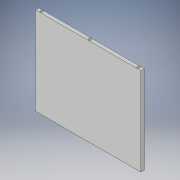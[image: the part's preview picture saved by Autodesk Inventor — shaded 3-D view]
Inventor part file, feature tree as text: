
AUTODESK INVENTOR PART (.ipt)
format: ipt  version: 2019 (Build 230136000, 136)  size: 108,544 bytes
history: native  units: mm
features: extrude x2, sketch x2
ambient origin geometry x8: Origin, YZ Plane, XZ Plane, XY Plane, X Axis, Y Axis, Z Axis, Center Point
bodies: Solid1 (feature_tree)
feature tree (4):
  extrude  "Extrusion1"  Depth=250.0mm
  extrude  "Extrusion2"  Depth=10.0mm
  sketch  "Sketch1"  dims[d0=300.0mm d1=250.0mm]
  sketch  "Sketch4"  dims[d2=162.5mm d3=125.0mm d4=10.0mm d5=0.0mm d6=7.0mm d7=7.0mm d8=7.0mm d9=12.0mm d10=12.0mm d12=150.0mm d13=5.0mm d14=5.0mm d15=5.0mm d16=10.0mm d17=0.0mm]
